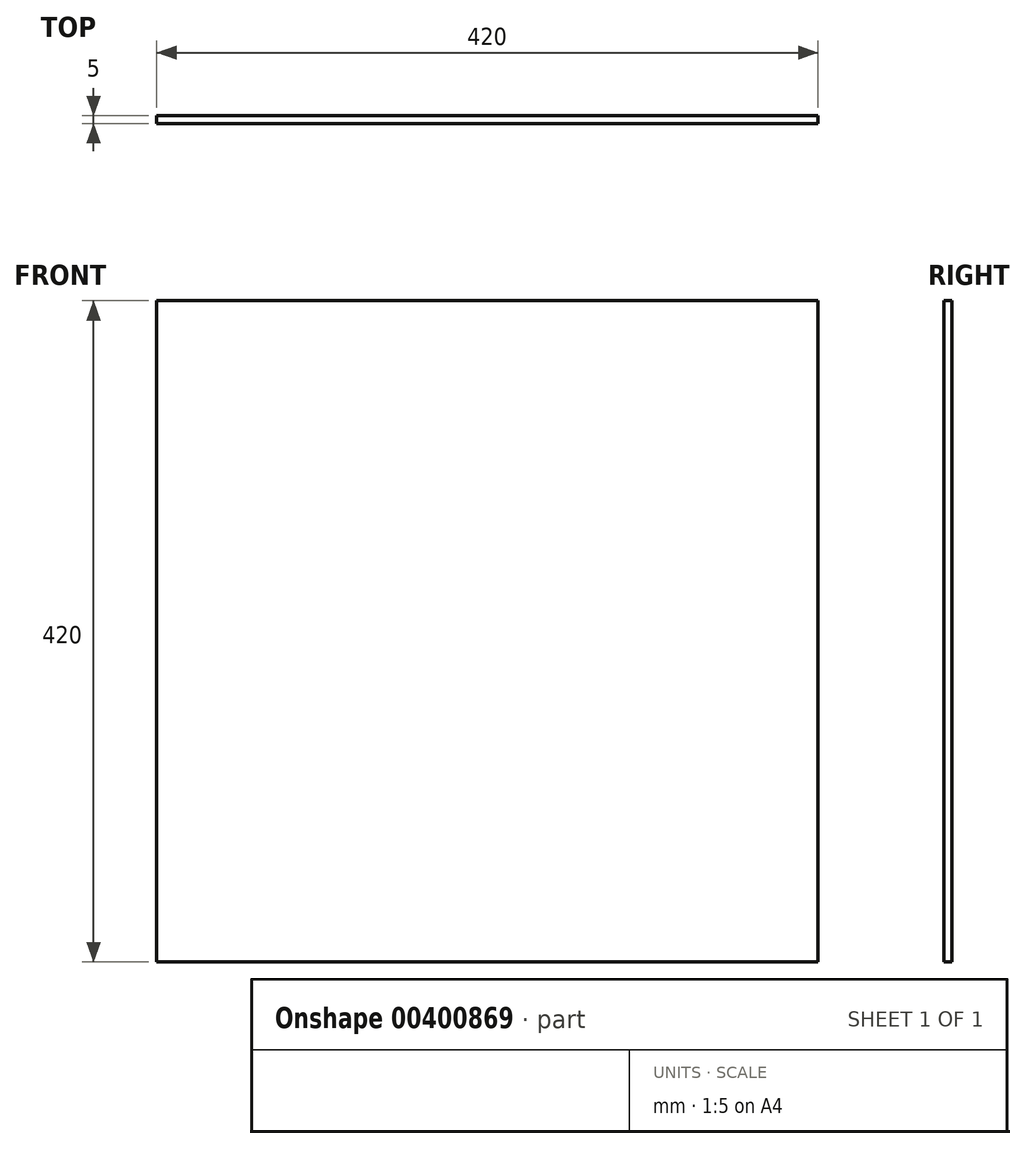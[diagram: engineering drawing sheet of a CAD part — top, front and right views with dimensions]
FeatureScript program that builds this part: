
annotation { "Feature Type Name" : "Feature", "Feature Type Description" : "" }
export const myFeature = defineFeature(function(context is Context, id is Id, definition is map)
    precondition{}
    {
        {
            var Q0;
            Q0=qCreatedBy(makeId("Front.planeOp"),FACE);
            var sketch = newSketch(context, id + "F0", { "sketchPlane" : qUnion([Q0])});
            skLineSegment(sketch, "E0", {"start": v(-210, 210) * mm, "end": v(210, 210) * mm});
            skLineSegment(sketch, "E1", {"start": v(210, 210) * mm, "end": v(210, -210) * mm});
            skLineSegment(sketch, "E2", {"start": v(210, -210) * mm, "end": v(-210, -210) * mm});
            skLineSegment(sketch, "E3", {"start": v(-210, 210) * mm, "end": v(-210, -210) * mm});
            skSolve(sketch);
        }
        {
            var Q0;
            Q0 = qSketchRegion(id + "F0", true);
            extrude(context, id + "F1", {"entities" : qUnion([Q0]), "depth" : 2.5 * mm});
        }
        {
            var Q0;
            Q0 = qSketchRegion(id + "F0", true);
            extrude(context, id + "F2", {"entities" : qUnion([Q0]), "operationType" : NewBodyOperationType.ADD, "oppositeDirection" : true, "depth" : 2.5 * mm});
        }
    });
